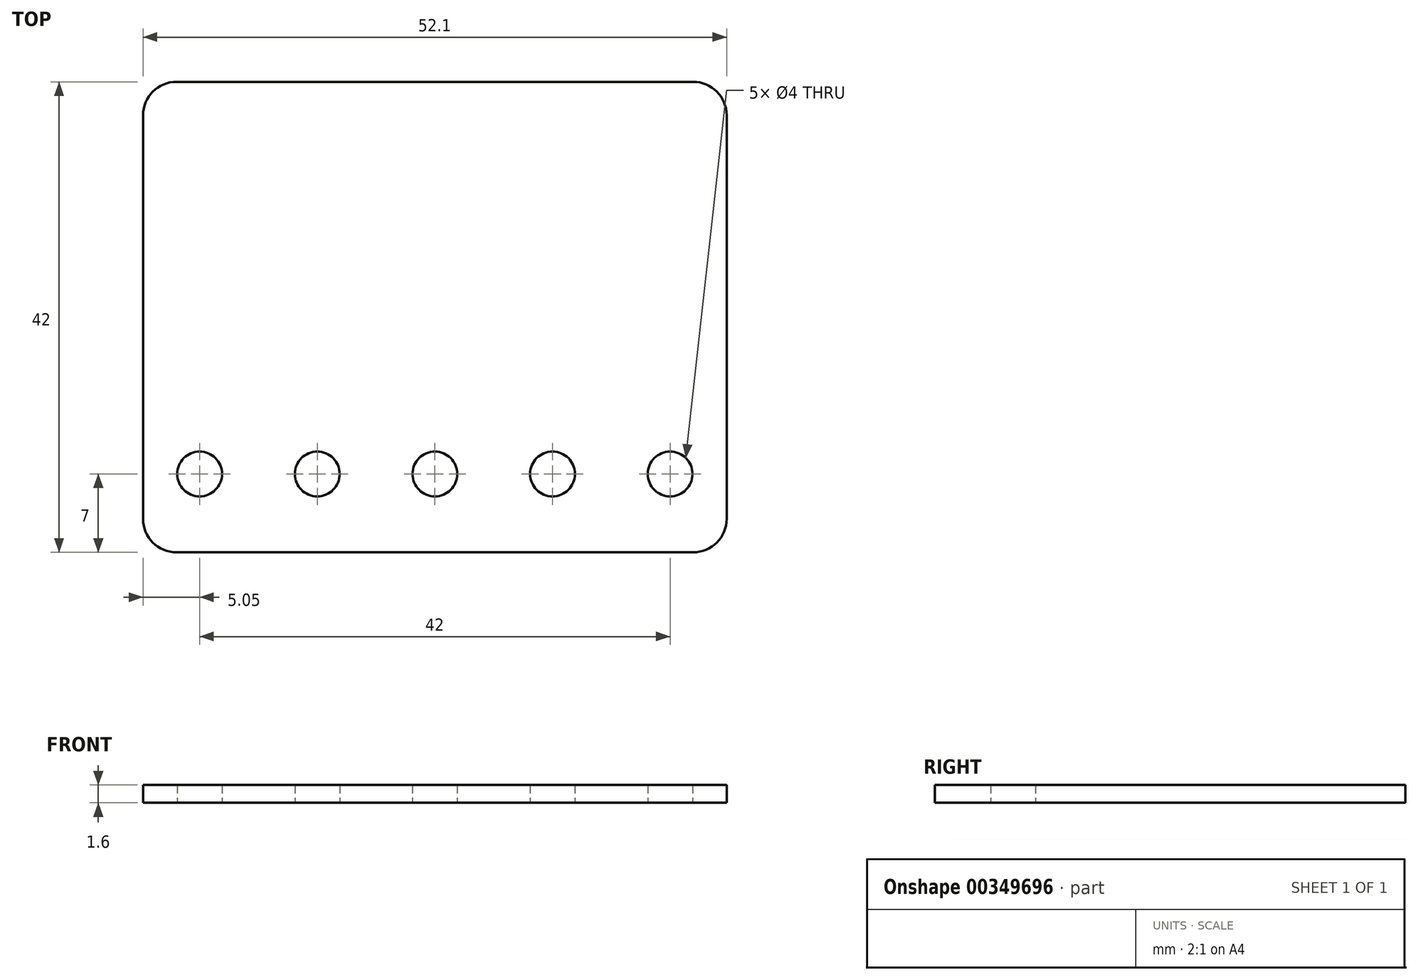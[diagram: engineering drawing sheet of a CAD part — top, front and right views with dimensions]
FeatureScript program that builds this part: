
annotation { "Feature Type Name" : "Feature", "Feature Type Description" : "" }
export const myFeature = defineFeature(function(context is Context, id is Id, definition is map)
    precondition{}
    {
        {
            var Q0;
            Q0=qCreatedBy(makeId("Top.planeOp"),FACE);
            var sketch = newSketch(context, id + "F0", { "sketchPlane" : qUnion([Q0])});
            skLineSegment(sketch, "E0.bottom", {"start": v(3, 0) * mm, "end": v(49.1, 0) * mm});
            skLineSegment(sketch, "E0.top", {"start": v(3, 42) * mm, "end": v(49.1, 42) * mm});
            skLineSegment(sketch, "E0.left", {"start": v(0, 3) * mm, "end": v(0, 39) * mm});
            skLineSegment(sketch, "E0.right", {"start": v(52.1, 3) * mm, "end": v(52.1, 39) * mm});
            skPoint(sketch, "E1.visualSharp", {"position": v(0, 42) * mm});
            skArc(sketch, "E1.filletArc", {"start": v(3, 42) * mm, "mid": v(0.88, 41.12) * mm, "end": v(0, 39) * mm});
            skPoint(sketch, "E2.visualSharp", {"position": v(52.1, 42) * mm});
            skArc(sketch, "E2.filletArc", {"start": v(52.1, 39) * mm, "mid": v(51.22, 41.12) * mm, "end": v(49.1, 42) * mm});
            skPoint(sketch, "E3.visualSharp", {"position": v(0, 0) * mm});
            skArc(sketch, "E3.filletArc", {"start": v(0, 3) * mm, "mid": v(0.88, 0.88) * mm, "end": v(3, 0) * mm});
            skPoint(sketch, "E4.visualSharp", {"position": v(52.1, 0) * mm});
            skArc(sketch, "E4.filletArc", {"start": v(49.1, 0) * mm, "mid": v(51.22, 0.88) * mm, "end": v(52.1, 3) * mm});
            skSolve(sketch);
        }
        {
            var Q0;
            Q0=makeQuery(id+"F0.imprint","IMPRINT",FACE,{"disambiguationData":[TD([[makeQuery(id+"F0.imprint","IMPRINT",EDGE,{"derivedFrom":sQuery(id+"F0.wireOp",EDGE,"E0.bottom")}),1.0]])]});
            extrude(context, id + "F1", {"entities" : qUnion([Q0]), "depth" : 1.6 * mm});
        }
        {
            var Q0;
            Q0=makeQuery(id+"F1.opExtrude","CAP_FACE",FACE,{"disambiguationData":[OSD([sQuery(id+"F0.wireOp",EDGE,"E0.bottom"),sQuery(id+"F0.wireOp",EDGE,"E0.top"),sQuery(id+"F0.wireOp",EDGE,"E0.left"),sQuery(id+"F0.wireOp",EDGE,"E0.right"),sQuery(id+"F0.wireOp",EDGE,"E1.filletArc"),sQuery(id+"F0.wireOp",EDGE,"E2.filletArc"),sQuery(id+"F0.wireOp",EDGE,"E3.filletArc"),sQuery(id+"F0.wireOp",EDGE,"E4.filletArc")])],"isStart":false});
            var sketch = newSketch(context, id + "F2", { "sketchPlane" : qUnion([Q0])});
            skPoint(sketch, "E5", {"position": v(26.05, 7) * mm});
            skPoint(sketch, "E5.positionSnap0", {"position": v(26.05, 0) * mm});
            skPoint(sketch, "E6", {"position": v(36.55, 7) * mm});
            skPoint(sketch, "E7", {"position": v(47.05, 7) * mm});
            skPoint(sketch, "E8", {"position": v(15.55, 7) * mm});
            skPoint(sketch, "E9", {"position": v(5.05, 7) * mm});
            skSolve(sketch);
        }
        {
            var Q0;
            Q0=sQuery(id+"F2.wireOp",VERTEX,"E9");
            var Q1;
            Q1=sQuery(id+"F2.wireOp",VERTEX,"E8");
            var Q2;
            Q2=sQuery(id+"F2.wireOp",VERTEX,"E5");
            var Q3;
            Q3=sQuery(id+"F2.wireOp",VERTEX,"E6");
            var Q4;
            Q4=sQuery(id+"F2.wireOp",VERTEX,"E7");
            var Q5;
            Q5=makeQuery(id+"F1.opExtrude","SWEPT_BODY",BODY,{"disambiguationData":[OSD([sQuery(id+"F0.wireOp",EDGE,"E0.bottom"),sQuery(id+"F0.wireOp",EDGE,"E0.top"),sQuery(id+"F0.wireOp",EDGE,"E0.left"),sQuery(id+"F0.wireOp",EDGE,"E0.right"),sQuery(id+"F0.wireOp",EDGE,"E1.filletArc"),sQuery(id+"F0.wireOp",EDGE,"E2.filletArc"),sQuery(id+"F0.wireOp",EDGE,"E3.filletArc"),sQuery(id+"F0.wireOp",EDGE,"E4.filletArc")])]});
            hole(context, id + "F3", {"style" : HoleStyle.SIMPLE, "endStyle" : HoleEndStyle.THROUGH, "holeDiameter" : 4 * mm, "isTappedThrough" : true, "tappedDepth" : 12 * mm, "tapClearance" : 3, "locations" : qUnion([Q0, Q1, Q2, Q3, Q4]), "scope" : qUnion([Q5])});
        }
    });
